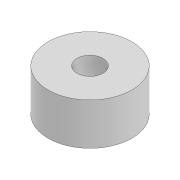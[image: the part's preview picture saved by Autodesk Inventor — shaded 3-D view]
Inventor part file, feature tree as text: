
AUTODESK INVENTOR PART (.ipt)
format: ipt  version: 2022 (Build 260153000, 153)  size: 84,480 bytes
history: native  units: mm
features: extrude x1, sketch x1
ambient origin geometry x8: Origin, YZ Plane, XZ Plane, XY Plane, X Axis, Y Axis, Z Axis, Center Point
bodies: Solid1 (feature_tree)
feature tree (2):
  extrude  "Extrusion1"  Depth=10.0mm
  sketch  "Sketch1"  dims[d0=3.1mm d1=10.0mm d2=5.0mm d3=0.0mm]
